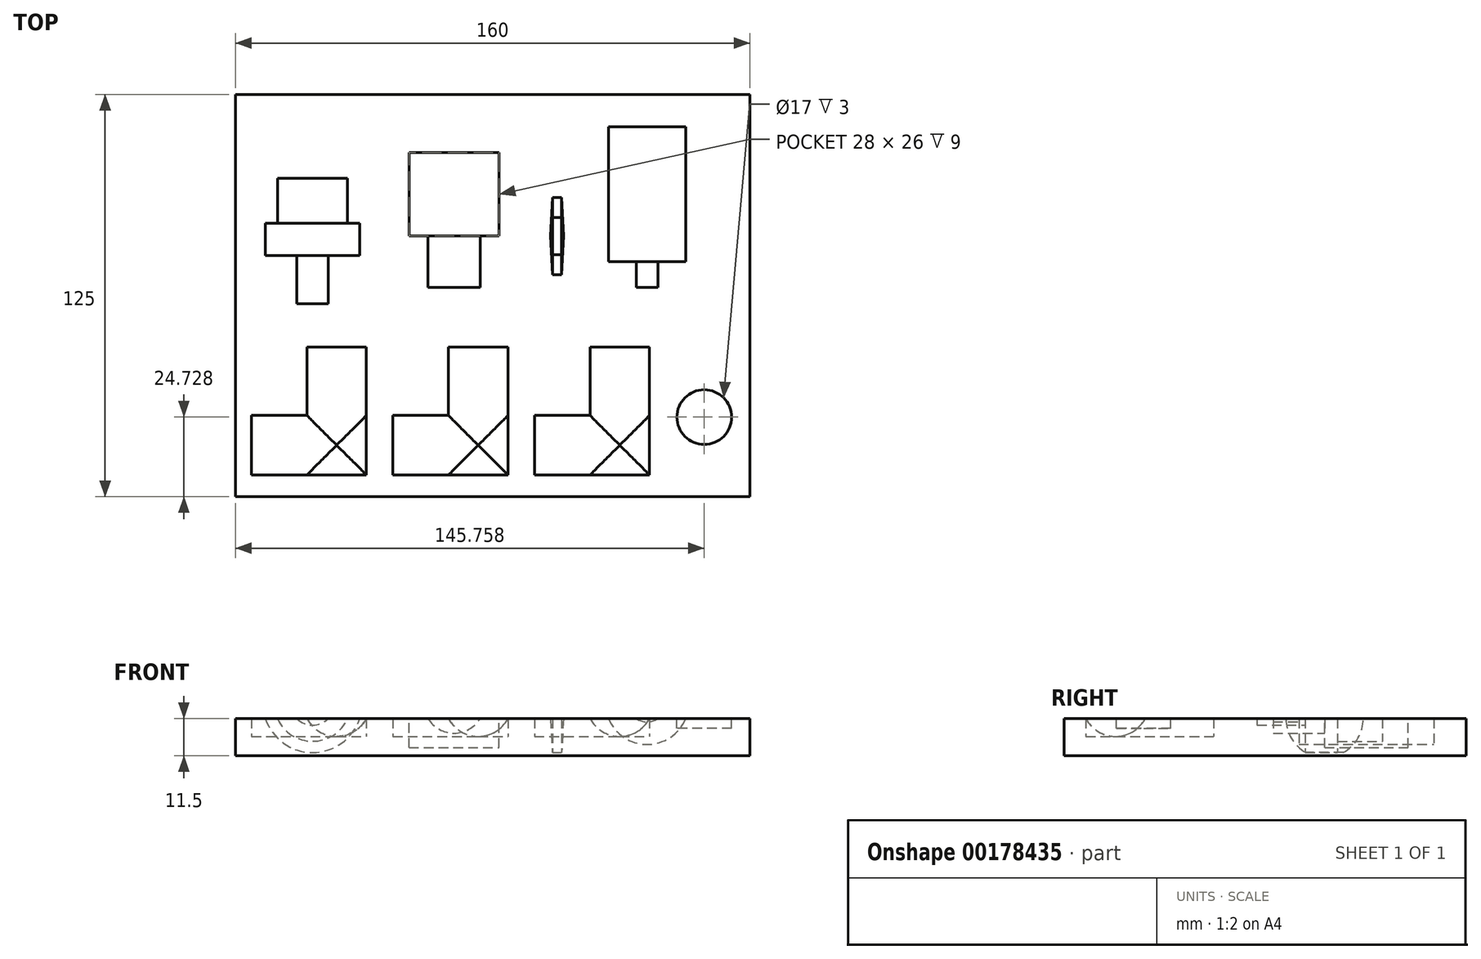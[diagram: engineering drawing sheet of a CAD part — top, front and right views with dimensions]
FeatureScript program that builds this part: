
annotation { "Feature Type Name" : "Feature", "Feature Type Description" : "" }
export const myFeature = defineFeature(function(context is Context, id is Id, definition is map)
    precondition{}
    {
        {
            var Q0;
            Q0=qCreatedBy(makeId("Top.planeOp"),FACE);
            var sketch = newSketch(context, id + "F0", { "sketchPlane" : qUnion([Q0])});
            skLineSegment(sketch, "E0.bottom", {"start": v(0, 0) * mm, "end": v(160, 0) * mm});
            skLineSegment(sketch, "E0.top", {"start": v(0, 125) * mm, "end": v(160, 125) * mm});
            skLineSegment(sketch, "E0.left", {"start": v(0, 0) * mm, "end": v(0, 125) * mm});
            skLineSegment(sketch, "E0.right", {"start": v(160, 0) * mm, "end": v(160, 125) * mm});
            skSolve(sketch);
        }
        {
            var Q0;
            Q0=makeQuery(id+"F0.imprint","IMPRINT",FACE,{"disambiguationData":[TD([[makeQuery(id+"F0.imprint","IMPRINT",EDGE,{"derivedFrom":sQuery(id+"F0.wireOp",EDGE,"E0.bottom")}),1.0]])]});
            extrude(context, id + "F1", {"entities" : qUnion([Q0]), "oppositeDirection" : true, "depth" : 16.5 * mm});
        }
        {
            var Q0;
            Q0=makeQuery(id+"F1.opExtrude","CAP_FACE",FACE,{"disambiguationData":[OSD([sQuery(id+"F0.wireOp",EDGE,"E0.bottom"),sQuery(id+"F0.wireOp",EDGE,"E0.top"),sQuery(id+"F0.wireOp",EDGE,"E0.left"),sQuery(id+"F0.wireOp",EDGE,"E0.right")])],"isStart":true});
            var sketch = newSketch(context, id + "F2", { "sketchPlane" : qUnion([Q0])});
            skLineSegment(sketch, "E1.bottom", {"start": v(0, 0) * mm, "end": v(5, 0) * mm, "construction": true});
            skLineSegment(sketch, "E1.top", {"start": v(0, 16) * mm, "end": v(5, 16) * mm, "construction": true});
            skLineSegment(sketch, "E1.left", {"start": v(0, 0) * mm, "end": v(0, 16) * mm, "construction": true});
            skLineSegment(sketch, "E1.right", {"start": v(5, 0) * mm, "end": v(5, 16) * mm, "construction": true});
            skLineSegment(sketch, "E2.bottom", {"start": v(5, 16) * mm, "end": v(42, 16) * mm});
            skLineSegment(sketch, "E2.top", {"start": v(5, 5.5) * mm, "end": v(42, 5.5) * mm});
            skLineSegment(sketch, "E2.left", {"start": v(5, 16) * mm, "end": v(5, 5.5) * mm});
            skLineSegment(sketch, "E2.right", {"start": v(42, 16) * mm, "end": v(42, 5.5) * mm});
            skLineSegment(sketch, "E3", {"start": v(42, 16) * mm, "end": v(49, 16) * mm, "construction": true});
            skLineSegment(sketch, "E4.bottom", {"start": v(49, 16) * mm, "end": v(86, 16) * mm});
            skLineSegment(sketch, "E4.top", {"start": v(49, 5.5) * mm, "end": v(86, 5.5) * mm});
            skLineSegment(sketch, "E4.left", {"start": v(49, 16) * mm, "end": v(49, 5.5) * mm});
            skLineSegment(sketch, "E4.right", {"start": v(86, 16) * mm, "end": v(86, 5.5) * mm});
            skLineSegment(sketch, "E5", {"start": v(86, 16) * mm, "end": v(93, 16) * mm, "construction": true});
            skLineSegment(sketch, "E6.bottom", {"start": v(93, 16) * mm, "end": v(130, 16) * mm});
            skLineSegment(sketch, "E6.top", {"start": v(93, 5.5) * mm, "end": v(130, 5.5) * mm});
            skLineSegment(sketch, "E6.left", {"start": v(93, 16) * mm, "end": v(93, 5.5) * mm});
            skLineSegment(sketch, "E6.right", {"start": v(130, 16) * mm, "end": v(130, 5.5) * mm});
            skSolve(sketch);
        }
        {
            var Q0;
            Q0 = qSketchRegion(id + "F2", true);
            var Q1;
            Q1=sQuery(id+"F2.wireOp",EDGE,"E2.bottom");
            revolve(context, id + "F3", {"operationType" : NewBodyOperationType.REMOVE, "entities" : qUnion([Q0]), "axis" : qUnion([Q1]), "revolveType" : RevolveType.FULL, "oppositeDirection" : true});
        }
        {
            var Q0;
            Q0=makeQuery(id+"F1.opExtrude","CAP_FACE",FACE,{"disambiguationData":[OSD([sQuery(id+"F0.wireOp",EDGE,"E0.bottom"),sQuery(id+"F0.wireOp",EDGE,"E0.top"),sQuery(id+"F0.wireOp",EDGE,"E0.left"),sQuery(id+"F0.wireOp",EDGE,"E0.right")])],"isStart":true});
            var sketch = newSketch(context, id + "F4", { "sketchPlane" : qUnion([Q0])});
            skLineSegment(sketch, "E7.bottom", {"start": v(0, 0) * mm, "end": v(31.5, 0) * mm, "construction": true});
            skLineSegment(sketch, "E7.top", {"start": v(0, 5.5) * mm, "end": v(31.5, 5.5) * mm, "construction": true});
            skLineSegment(sketch, "E7.left", {"start": v(0, 0) * mm, "end": v(0, 5.5) * mm, "construction": true});
            skLineSegment(sketch, "E7.right", {"start": v(31.5, 0) * mm, "end": v(31.5, 5.5) * mm, "construction": true});
            skLineSegment(sketch, "E8.bottom", {"start": v(31.5, 5.5) * mm, "end": v(42, 5.5) * mm});
            skLineSegment(sketch, "E8.top", {"start": v(31.5, 46.5) * mm, "end": v(42, 46.5) * mm});
            skLineSegment(sketch, "E8.left", {"start": v(31.5, 5.5) * mm, "end": v(31.5, 46.5) * mm});
            skLineSegment(sketch, "E8.right", {"start": v(42, 5.5) * mm, "end": v(42, 46.5) * mm});
            skSolve(sketch);
        }
        {
            var Q0;
            Q0 = qSketchRegion(id + "F4", true);
            var Q1;
            Q1=sQuery(id+"F4.wireOp",EDGE,"E8.left");
            revolve(context, id + "F5", {"operationType" : NewBodyOperationType.REMOVE, "entities" : qUnion([Q0]), "axis" : qUnion([Q1]), "revolveType" : RevolveType.FULL, "oppositeDirection" : true});
        }
        {
            var Q0;
            Q0=makeQuery(id+"F1.opExtrude","CAP_FACE",FACE,{"disambiguationData":[OSD([sQuery(id+"F0.wireOp",EDGE,"E0.bottom"),sQuery(id+"F0.wireOp",EDGE,"E0.top"),sQuery(id+"F0.wireOp",EDGE,"E0.left"),sQuery(id+"F0.wireOp",EDGE,"E0.right")])],"isStart":true});
            var sketch = newSketch(context, id + "F6", { "sketchPlane" : qUnion([Q0])});
            skLineSegment(sketch, "E9.bottom", {"start": v(0, 0) * mm, "end": v(75.5, 0) * mm, "construction": true});
            skLineSegment(sketch, "E9.top", {"start": v(0, 5.5) * mm, "end": v(75.5, 5.5) * mm, "construction": true});
            skLineSegment(sketch, "E9.left", {"start": v(0, 0) * mm, "end": v(0, 5.5) * mm, "construction": true});
            skLineSegment(sketch, "E9.right", {"start": v(75.5, 0) * mm, "end": v(75.5, 5.5) * mm, "construction": true});
            skLineSegment(sketch, "E10.bottom", {"start": v(75.5, 5.5) * mm, "end": v(86, 5.5) * mm});
            skLineSegment(sketch, "E10.top", {"start": v(75.5, 46.5) * mm, "end": v(86, 46.5) * mm});
            skLineSegment(sketch, "E10.left", {"start": v(75.5, 5.5) * mm, "end": v(75.5, 46.5) * mm});
            skLineSegment(sketch, "E10.right", {"start": v(86, 5.5) * mm, "end": v(86, 46.5) * mm});
            skSolve(sketch);
        }
        {
            var Q0;
            Q0 = qSketchRegion(id + "F6", true);
            var Q1;
            Q1=sQuery(id+"F6.wireOp",EDGE,"E10.left");
            revolve(context, id + "F7", {"operationType" : NewBodyOperationType.REMOVE, "entities" : qUnion([Q0]), "axis" : qUnion([Q1]), "revolveType" : RevolveType.FULL, "oppositeDirection" : true});
        }
        {
            var Q0;
            Q0=makeQuery(id+"F1.opExtrude","CAP_FACE",FACE,{"disambiguationData":[OSD([sQuery(id+"F0.wireOp",EDGE,"E0.bottom"),sQuery(id+"F0.wireOp",EDGE,"E0.top"),sQuery(id+"F0.wireOp",EDGE,"E0.left"),sQuery(id+"F0.wireOp",EDGE,"E0.right")])],"isStart":true});
            var sketch = newSketch(context, id + "F8", { "sketchPlane" : qUnion([Q0])});
            skLineSegment(sketch, "E11.bottom", {"start": v(0, 0) * mm, "end": v(119.5, 0) * mm, "construction": true});
            skLineSegment(sketch, "E11.top", {"start": v(0, 5.5) * mm, "end": v(119.5, 5.5) * mm, "construction": true});
            skLineSegment(sketch, "E11.left", {"start": v(0, 0) * mm, "end": v(0, 5.5) * mm, "construction": true});
            skLineSegment(sketch, "E11.right", {"start": v(119.5, 0) * mm, "end": v(119.5, 5.5) * mm, "construction": true});
            skLineSegment(sketch, "E12.bottom", {"start": v(119.5, 5.5) * mm, "end": v(130, 5.5) * mm});
            skLineSegment(sketch, "E12.top", {"start": v(119.5, 46.5) * mm, "end": v(130, 46.5) * mm});
            skLineSegment(sketch, "E12.left", {"start": v(119.5, 5.5) * mm, "end": v(119.5, 46.5) * mm});
            skLineSegment(sketch, "E12.right", {"start": v(130, 5.5) * mm, "end": v(130, 46.5) * mm});
            skSolve(sketch);
        }
        {
            var Q0;
            Q0 = qSketchRegion(id + "F8", true);
            var Q1;
            Q1=sQuery(id+"F8.wireOp",EDGE,"E12.left");
            revolve(context, id + "F9", {"operationType" : NewBodyOperationType.REMOVE, "entities" : qUnion([Q0]), "axis" : qUnion([Q1]), "revolveType" : RevolveType.FULL, "oppositeDirection" : true});
        }
        {
            var Q0;
            Q0=makeQuery(id+"F1.opExtrude","CAP_FACE",FACE,{"disambiguationData":[OSD([sQuery(id+"F0.wireOp",EDGE,"E0.bottom"),sQuery(id+"F0.wireOp",EDGE,"E0.top"),sQuery(id+"F0.wireOp",EDGE,"E0.left"),sQuery(id+"F0.wireOp",EDGE,"E0.right")])],"isStart":true});
            var sketch = newSketch(context, id + "F10", { "sketchPlane" : qUnion([Q0])});
            skCircle(sketch, "E13", {"center": v(145.76, 24.73) * mm, "radius": 8.5 * mm});
            skSolve(sketch);
        }
        {
            var Q0;
            Q0 = qSketchRegion(id + "F10", true);
            extrude(context, id + "F11", {"entities" : qUnion([Q0]), "operationType" : NewBodyOperationType.REMOVE, "oppositeDirection" : true, "depth" : 8 * mm});
        }
        {
            var Q0;
            Q0=makeQuery(id+"F1.opExtrude","CAP_FACE",FACE,{"disambiguationData":[OSD([sQuery(id+"F0.wireOp",EDGE,"E0.bottom"),sQuery(id+"F0.wireOp",EDGE,"E0.top"),sQuery(id+"F0.wireOp",EDGE,"E0.left"),sQuery(id+"F0.wireOp",EDGE,"E0.right")])],"isStart":true});
            var sketch = newSketch(context, id + "F12", { "sketchPlane" : qUnion([Q0])});
            skLineSegment(sketch, "E14.bottom", {"start": v(0, 0) * mm, "end": v(24, 0) * mm, "construction": true});
            skLineSegment(sketch, "E14.top", {"start": v(0, 60) * mm, "end": v(24, 60) * mm, "construction": true});
            skLineSegment(sketch, "E14.left", {"start": v(0, 0) * mm, "end": v(0, 60) * mm, "construction": true});
            skLineSegment(sketch, "E14.right", {"start": v(24, 0) * mm, "end": v(24, 60) * mm, "construction": true});
            skLineSegment(sketch, "E15.bottom", {"start": v(24, 60) * mm, "end": v(31, 60) * mm});
            skLineSegment(sketch, "E15.left", {"start": v(24, 60) * mm, "end": v(24, 75) * mm});
            skLineSegment(sketch, "E15.right", {"start": v(31, 60) * mm, "end": v(31, 75) * mm});
            skLineSegment(sketch, "E16.bottom", {"start": v(31, 75) * mm, "end": v(39.5, 75) * mm});
            skLineSegment(sketch, "E16.top", {"start": v(36, 85) * mm, "end": v(39.5, 85) * mm});
            skLineSegment(sketch, "E16.left", {"start": v(24, 75) * mm, "end": v(24, 85) * mm});
            skLineSegment(sketch, "E16.right", {"start": v(39.5, 75) * mm, "end": v(39.5, 85) * mm});
            skLineSegment(sketch, "E17.top", {"start": v(28.5, 99) * mm, "end": v(36, 99) * mm});
            skLineSegment(sketch, "E17.left", {"start": v(24, 85) * mm, "end": v(24, 99) * mm});
            skLineSegment(sketch, "E17.right", {"start": v(36, 85) * mm, "end": v(36, 99) * mm});
            skLineSegment(sketch, "E18.top", {"start": v(24, 113) * mm, "end": v(28.5, 113) * mm});
            skLineSegment(sketch, "E18.left", {"start": v(24, 99) * mm, "end": v(24, 113) * mm});
            skLineSegment(sketch, "E18.right", {"start": v(28.5, 99) * mm, "end": v(28.5, 113) * mm});
            skSolve(sketch);
        }
        {
            var Q0;
            Q0 = qSketchRegion(id + "F12", true);
            var Q1;
            Q1=sQuery(id+"F12.wireOp",EDGE,"E17.left");
            revolve(context, id + "F13", {"operationType" : NewBodyOperationType.REMOVE, "entities" : qUnion([Q0]), "axis" : qUnion([Q1]), "revolveType" : RevolveType.FULL, "oppositeDirection" : true});
        }
        {
            var Q0;
            Q0=makeQuery(id+"F1.opExtrude","CAP_FACE",FACE,{"disambiguationData":[OSD([sQuery(id+"F0.wireOp",EDGE,"E0.bottom"),sQuery(id+"F0.wireOp",EDGE,"E0.top"),sQuery(id+"F0.wireOp",EDGE,"E0.left"),sQuery(id+"F0.wireOp",EDGE,"E0.right")])],"isStart":true});
            var sketch = newSketch(context, id + "F14", { "sketchPlane" : qUnion([Q0])});
            skLineSegment(sketch, "E19.bottom", {"start": v(0, 0) * mm, "end": v(68, 0) * mm, "construction": true});
            skLineSegment(sketch, "E19.top", {"start": v(0, 65) * mm, "end": v(68, 65) * mm, "construction": true});
            skLineSegment(sketch, "E19.left", {"start": v(0, 0) * mm, "end": v(0, 65) * mm, "construction": true});
            skLineSegment(sketch, "E19.right", {"start": v(68, 0) * mm, "end": v(68, 65) * mm, "construction": true});
            skLineSegment(sketch, "E20.bottom", {"start": v(68, 65) * mm, "end": v(77.5, 65) * mm});
            skLineSegment(sketch, "E20.top", {"start": v(68, 81) * mm, "end": v(77.5, 81) * mm});
            skLineSegment(sketch, "E20.left", {"start": v(68, 65) * mm, "end": v(68, 81) * mm});
            skLineSegment(sketch, "E20.right", {"start": v(77.5, 65) * mm, "end": v(77.5, 81) * mm});
            skSolve(sketch);
        }
        {
            var Q0;
            Q0 = qSketchRegion(id + "F14", true);
            var Q1;
            Q1=sQuery(id+"F14.wireOp",EDGE,"E20.left");
            revolve(context, id + "F15", {"operationType" : NewBodyOperationType.REMOVE, "entities" : qUnion([Q0]), "axis" : qUnion([Q1]), "revolveType" : RevolveType.FULL, "oppositeDirection" : true});
        }
        {
            var Q0;
            Q0=makeQuery(id+"F1.opExtrude","CAP_FACE",FACE,{"disambiguationData":[OSD([sQuery(id+"F0.wireOp",EDGE,"E0.bottom"),sQuery(id+"F0.wireOp",EDGE,"E0.top"),sQuery(id+"F0.wireOp",EDGE,"E0.left"),sQuery(id+"F0.wireOp",EDGE,"E0.right")])],"isStart":true});
            var sketch = newSketch(context, id + "F16", { "sketchPlane" : qUnion([Q0])});
            skLineSegment(sketch, "E21.bottom", {"start": v(0, 0) * mm, "end": v(54, 0) * mm, "construction": true});
            skLineSegment(sketch, "E21.top", {"start": v(0, 81) * mm, "end": v(54, 81) * mm, "construction": true});
            skLineSegment(sketch, "E21.left", {"start": v(0, 0) * mm, "end": v(0, 81) * mm, "construction": true});
            skLineSegment(sketch, "E21.right", {"start": v(54, 0) * mm, "end": v(54, 81) * mm, "construction": true});
            skLineSegment(sketch, "E22.bottom", {"start": v(54, 81) * mm, "end": v(82, 81) * mm});
            skLineSegment(sketch, "E22.top", {"start": v(54, 107) * mm, "end": v(82, 107) * mm});
            skLineSegment(sketch, "E22.left", {"start": v(54, 81) * mm, "end": v(54, 107) * mm});
            skLineSegment(sketch, "E22.right", {"start": v(82, 81) * mm, "end": v(82, 107) * mm});
            skSolve(sketch);
        }
        {
            var Q0;
            Q0=makeQuery(id+"F16.imprint","IMPRINT",FACE,{"disambiguationData":[TD([[makeQuery(id+"F16.imprint","IMPRINT",EDGE,{"derivedFrom":sQuery(id+"F16.wireOp",EDGE,"E22.top")}),-1.0]])]});
            extrude(context, id + "F17", {"entities" : qUnion([Q0]), "operationType" : NewBodyOperationType.REMOVE, "oppositeDirection" : true, "depth" : 14 * mm});
        }
        {
            var Q0;
            Q0=makeQuery(id+"F1.opExtrude","CAP_FACE",FACE,{"disambiguationData":[OSD([sQuery(id+"F0.wireOp",EDGE,"E0.bottom"),sQuery(id+"F0.wireOp",EDGE,"E0.top"),sQuery(id+"F0.wireOp",EDGE,"E0.left"),sQuery(id+"F0.wireOp",EDGE,"E0.right")])],"isStart":true});
            var sketch = newSketch(context, id + "F18", { "sketchPlane" : qUnion([Q0])});
            skLineSegment(sketch, "E23.bottom", {"start": v(0, 0) * mm, "end": v(128, 0) * mm, "construction": true});
            skLineSegment(sketch, "E23.top", {"start": v(0, 65) * mm, "end": v(128, 65) * mm, "construction": true});
            skLineSegment(sketch, "E23.left", {"start": v(0, 0) * mm, "end": v(0, 65) * mm, "construction": true});
            skLineSegment(sketch, "E23.right", {"start": v(128, 0) * mm, "end": v(128, 65) * mm, "construction": true});
            skLineSegment(sketch, "E24.bottom", {"start": v(128, 65) * mm, "end": v(134, 65) * mm});
            skLineSegment(sketch, "E24.left", {"start": v(128, 65) * mm, "end": v(128, 73) * mm});
            skLineSegment(sketch, "E24.right", {"start": v(134, 65) * mm, "end": v(134, 73) * mm});
            skLineSegment(sketch, "E25.bottom", {"start": v(134, 73) * mm, "end": v(141, 73) * mm});
            skLineSegment(sketch, "E25.top", {"start": v(128, 115) * mm, "end": v(141, 115) * mm});
            skLineSegment(sketch, "E25.left", {"start": v(128, 73) * mm, "end": v(128, 115) * mm});
            skLineSegment(sketch, "E25.right", {"start": v(141, 73) * mm, "end": v(141, 115) * mm});
            skSolve(sketch);
        }
        {
            var Q0;
            Q0=makeQuery(id+"F18.imprint","IMPRINT",FACE,{"disambiguationData":[TD([[makeQuery(id+"F18.imprint","IMPRINT",EDGE,{"derivedFrom":sQuery(id+"F18.wireOp",EDGE,"E24.bottom")}),1.0]])]});
            var Q1;
            Q1=sQuery(id+"F18.wireOp",EDGE,"E25.left");
            revolve(context, id + "F19", {"operationType" : NewBodyOperationType.REMOVE, "entities" : qUnion([Q0]), "axis" : qUnion([Q1]), "revolveType" : RevolveType.FULL, "oppositeDirection" : true});
        }
        {
            var Q0;
            Q0=qCreatedBy(makeId("Front.planeOp"),FACE);
            var sketch = newSketch(context, id + "F20", { "sketchPlane" : qUnion([Q0])});
            skLineSegment(sketch, "E26.bottom", {"start": v(0, 0) * mm, "end": v(160, 0) * mm});
            skLineSegment(sketch, "E26.top", {"start": v(0, -5) * mm, "end": v(160, -5) * mm});
            skLineSegment(sketch, "E26.left", {"start": v(0, 0) * mm, "end": v(0, -5) * mm});
            skLineSegment(sketch, "E26.right", {"start": v(160, 0) * mm, "end": v(160, -5) * mm});
            skSolve(sketch);
        }
        {
            var Q0;
            Q0=makeQuery(id+"F20.imprint","IMPRINT",FACE,{"disambiguationData":[TD([[makeQuery(id+"F20.imprint","IMPRINT",EDGE,{"derivedFrom":sQuery(id+"F20.wireOp",EDGE,"E26.bottom")}),-1.0]])]});
            extrude(context, id + "F21", {"entities" : qUnion([Q0]), "operationType" : NewBodyOperationType.REMOVE, "oppositeDirection" : true, "depth" : 150 * mm});
        }
        {
            var Q0;
            Q0=makeQuery(id+"F21.boolean.opBoolean","COPY",FACE,{"derivedFrom":makeQuery(id+"F21.opExtrude","SWEPT_FACE",FACE,{"disambiguationData":[OSD([sQuery(id+"F20.wireOp",EDGE,"E26.top")])]})});
            var sketch = newSketch(context, id + "F22", { "sketchPlane" : qUnion([Q0])});
            skLineSegment(sketch, "E27.bottom", {"start": v(0, 0) * mm, "end": v(98, 0) * mm, "construction": true});
            skLineSegment(sketch, "E27.top", {"start": v(0, 81) * mm, "end": v(98, 81) * mm, "construction": true});
            skLineSegment(sketch, "E27.left", {"start": v(0, 0) * mm, "end": v(0, 81) * mm, "construction": true});
            skLineSegment(sketch, "E27.right", {"start": v(98, 0) * mm, "end": v(98, 81) * mm, "construction": true});
            skLineSegment(sketch, "E28.bottom", {"start": v(98, 81) * mm, "end": v(102, 81) * mm});
            skLineSegment(sketch, "E28.top", {"start": v(98.63, 93) * mm, "end": v(101.37, 93) * mm});
            skLineSegment(sketch, "E29", {"start": v(98, 81) * mm, "end": v(98.63, 93) * mm});
            skLineSegment(sketch, "E30", {"start": v(102, 81) * mm, "end": v(101.37, 93) * mm});
            skSolve(sketch);
        }
        {
            var Q0;
            Q0=makeQuery(id+"F22.imprint","IMPRINT",FACE,{"disambiguationData":[TD([[makeQuery(id+"F22.imprint","IMPRINT",EDGE,{"derivedFrom":sQuery(id+"F22.wireOp",EDGE,"E28.bottom")}),1.0]])]});
            var Q1;
            Q1=sQuery(id+"F22.wireOp",EDGE,"E28.bottom");
            revolve(context, id + "F23", {"operationType" : NewBodyOperationType.REMOVE, "entities" : qUnion([Q0]), "axis" : qUnion([Q1]), "revolveType" : RevolveType.FULL, "oppositeDirection" : true});
        }
        {
            var Q0;
            Q0=makeQuery(id+"F21.boolean.opBoolean","COPY",FACE,{"derivedFrom":makeQuery(id+"F21.opExtrude","SWEPT_FACE",FACE,{"disambiguationData":[OSD([sQuery(id+"F20.wireOp",EDGE,"E26.top")])]})});
            var sketch = newSketch(context, id + "F24", { "sketchPlane" : qUnion([Q0])});
            skLineSegment(sketch, "E31.bottom", {"start": v(40.73, 25.23) * mm, "end": v(42, 25.23) * mm});
            skLineSegment(sketch, "E31.top", {"start": v(40.73, 6.77) * mm, "end": v(42, 6.77) * mm});
            skLineSegment(sketch, "E31.left", {"start": v(40.73, 25.23) * mm, "end": v(40.73, 6.77) * mm});
            skLineSegment(sketch, "E31.right", {"start": v(42, 25.23) * mm, "end": v(42, 6.77) * mm});
            skLineSegment(sketch, "E32.bottom", {"start": v(22.27, 5.5) * mm, "end": v(40.73, 5.5) * mm});
            skLineSegment(sketch, "E32.top", {"start": v(22.27, 6.77) * mm, "end": v(40.73, 6.77) * mm});
            skLineSegment(sketch, "E32.left", {"start": v(22.27, 5.5) * mm, "end": v(22.27, 6.77) * mm});
            skLineSegment(sketch, "E32.right", {"start": v(40.73, 5.5) * mm, "end": v(40.73, 6.77) * mm});
            skLineSegment(sketch, "E33.bottom", {"start": v(66.27, 6.77) * mm, "end": v(84.73, 6.77) * mm});
            skLineSegment(sketch, "E33.top", {"start": v(66.27, 5.5) * mm, "end": v(84.73, 5.5) * mm});
            skLineSegment(sketch, "E33.left", {"start": v(66.27, 6.77) * mm, "end": v(66.27, 5.5) * mm});
            skLineSegment(sketch, "E33.right", {"start": v(84.73, 6.77) * mm, "end": v(84.73, 5.5) * mm});
            skLineSegment(sketch, "E34.bottom", {"start": v(86, 6.77) * mm, "end": v(84.73, 6.77) * mm});
            skLineSegment(sketch, "E34.top", {"start": v(86, 25.23) * mm, "end": v(84.73, 25.23) * mm});
            skLineSegment(sketch, "E34.left", {"start": v(86, 6.77) * mm, "end": v(86, 25.23) * mm});
            skLineSegment(sketch, "E34.right", {"start": v(84.73, 6.77) * mm, "end": v(84.73, 25.23) * mm});
            skLineSegment(sketch, "E35.bottom", {"start": v(110.27, 6.77) * mm, "end": v(128.73, 6.77) * mm});
            skLineSegment(sketch, "E35.top", {"start": v(110.27, 5.5) * mm, "end": v(128.73, 5.5) * mm});
            skLineSegment(sketch, "E35.left", {"start": v(110.27, 6.77) * mm, "end": v(110.27, 5.5) * mm});
            skLineSegment(sketch, "E35.right", {"start": v(128.73, 6.77) * mm, "end": v(128.73, 5.5) * mm});
            skLineSegment(sketch, "E36.bottom", {"start": v(130, 6.77) * mm, "end": v(128.73, 6.77) * mm});
            skLineSegment(sketch, "E36.top", {"start": v(130, 25.23) * mm, "end": v(128.73, 25.23) * mm});
            skLineSegment(sketch, "E36.left", {"start": v(130, 6.77) * mm, "end": v(130, 25.23) * mm});
            skLineSegment(sketch, "E36.right", {"start": v(128.73, 6.77) * mm, "end": v(128.73, 25.23) * mm});
            skSolve(sketch);
        }
        {
            var Q0;
            Q0 = qSketchRegion(id + "F24", true);
            extrude(context, id + "F25", {"entities" : qUnion([Q0]), "operationType" : NewBodyOperationType.ADD, "oppositeDirection" : true, "depth" : 10 * mm});
        }
        {
            var Q0;
            Q0=makeQuery(id+"F25.boolean.opBoolean","MERGE",FACE,{"derivedFrom":[makeQuery(id+"F21.boolean.opBoolean","COPY",FACE,{"derivedFrom":makeQuery(id+"F21.opExtrude","SWEPT_FACE",FACE,{"disambiguationData":[OSD([sQuery(id+"F20.wireOp",EDGE,"E26.top")])]})}),makeQuery(id+"F25.opExtrude","CAP_FACE",FACE,{"disambiguationData":[OSD([sQuery(id+"F24.wireOp",EDGE,"E31.bottom"),sQuery(id+"F24.wireOp",EDGE,"E31.top"),sQuery(id+"F24.wireOp",EDGE,"E31.left"),sQuery(id+"F24.wireOp",EDGE,"E31.right")])],"isStart":true}),makeQuery(id+"F25.opExtrude","CAP_FACE",FACE,{"disambiguationData":[OSD([sQuery(id+"F24.wireOp",EDGE,"E32.bottom"),sQuery(id+"F24.wireOp",EDGE,"E32.top"),sQuery(id+"F24.wireOp",EDGE,"E32.left"),sQuery(id+"F24.wireOp",EDGE,"E32.right")])],"isStart":true}),makeQuery(id+"F25.opExtrude","CAP_FACE",FACE,{"disambiguationData":[OSD([sQuery(id+"F24.wireOp",EDGE,"E33.bottom"),sQuery(id+"F24.wireOp",EDGE,"E33.top"),sQuery(id+"F24.wireOp",EDGE,"E33.left"),sQuery(id+"F24.wireOp",EDGE,"E33.right")])],"isStart":true}),makeQuery(id+"F25.opExtrude","CAP_FACE",FACE,{"disambiguationData":[OSD([sQuery(id+"F24.wireOp",EDGE,"E34.bottom"),sQuery(id+"F24.wireOp",EDGE,"E34.top"),sQuery(id+"F24.wireOp",EDGE,"E34.left"),sQuery(id+"F24.wireOp",EDGE,"E34.right")])],"isStart":true}),makeQuery(id+"F25.opExtrude","CAP_FACE",FACE,{"disambiguationData":[OSD([sQuery(id+"F24.wireOp",EDGE,"E35.bottom"),sQuery(id+"F24.wireOp",EDGE,"E35.top"),sQuery(id+"F24.wireOp",EDGE,"E35.left"),sQuery(id+"F24.wireOp",EDGE,"E35.right")])],"isStart":true}),makeQuery(id+"F25.opExtrude","CAP_FACE",FACE,{"disambiguationData":[OSD([sQuery(id+"F24.wireOp",EDGE,"E36.bottom"),sQuery(id+"F24.wireOp",EDGE,"E36.top"),sQuery(id+"F24.wireOp",EDGE,"E36.left"),sQuery(id+"F24.wireOp",EDGE,"E36.right")])],"isStart":true})]});
            var sketch = newSketch(context, id + "F26", { "sketchPlane" : qUnion([Q0])});
            skLineSegment(sketch, "E37.bottom", {"start": v(96.36, 90) * mm, "end": v(104.08, 90) * mm});
            skLineSegment(sketch, "E37.top", {"start": v(96.36, 74.21) * mm, "end": v(104.08, 74.21) * mm});
            skLineSegment(sketch, "E37.left", {"start": v(96.36, 90) * mm, "end": v(96.36, 74.21) * mm});
            skLineSegment(sketch, "E37.right", {"start": v(104.08, 90) * mm, "end": v(104.08, 74.21) * mm});
            skSolve(sketch);
        }
        {
            var Q0;
            {var subQ0=makeQuery(id+"F23.opRevolve","SWEPT_FACE",FACE,{"disambiguationData":[OSD([sQuery(id+"F22.wireOp",EDGE,"E29")])]});var subQ1=makeQuery(id+"F21.boolean.opBoolean","COPY",FACE,{"derivedFrom":makeQuery(id+"F21.opExtrude","SWEPT_FACE",FACE,{"disambiguationData":[OSD([sQuery(id+"F20.wireOp",EDGE,"E26.top")])]})});var subQ2=makeQuery(id+"F23.boolean.opBoolean","INTERSECT",EDGE,{"disambiguationData":[OD(1.0)],"derivedFrom":[subQ1,subQ0]});var subQ5=sQuery(id+"F26.wireOp",EDGE,"E37.bottom");var subQ6=makeQuery(id+"F26.imprint","INTERSECT",VERTEX,{"derivedFrom":[subQ2,subQ5]});Q0=makeQuery(id+"F26.imprint","IMPRINT",FACE,{"disambiguationData":[TD([[makeQuery(id+"F26.imprint","IMPRINT",EDGE,{"disambiguationData":[TD([[subQ6,-1.0]])],"derivedFrom":subQ5}),-1.0]])]});}
            extrude(context, id + "F27", {"entities" : qUnion([Q0]), "operationType" : NewBodyOperationType.ADD, "oppositeDirection" : true, "depth" : 11.5 * mm, "hasSecondDirection" : true, "secondDirectionOppositeDirection" : true, "secondDirectionDepth" : 10.5 * mm});
        }
    });
